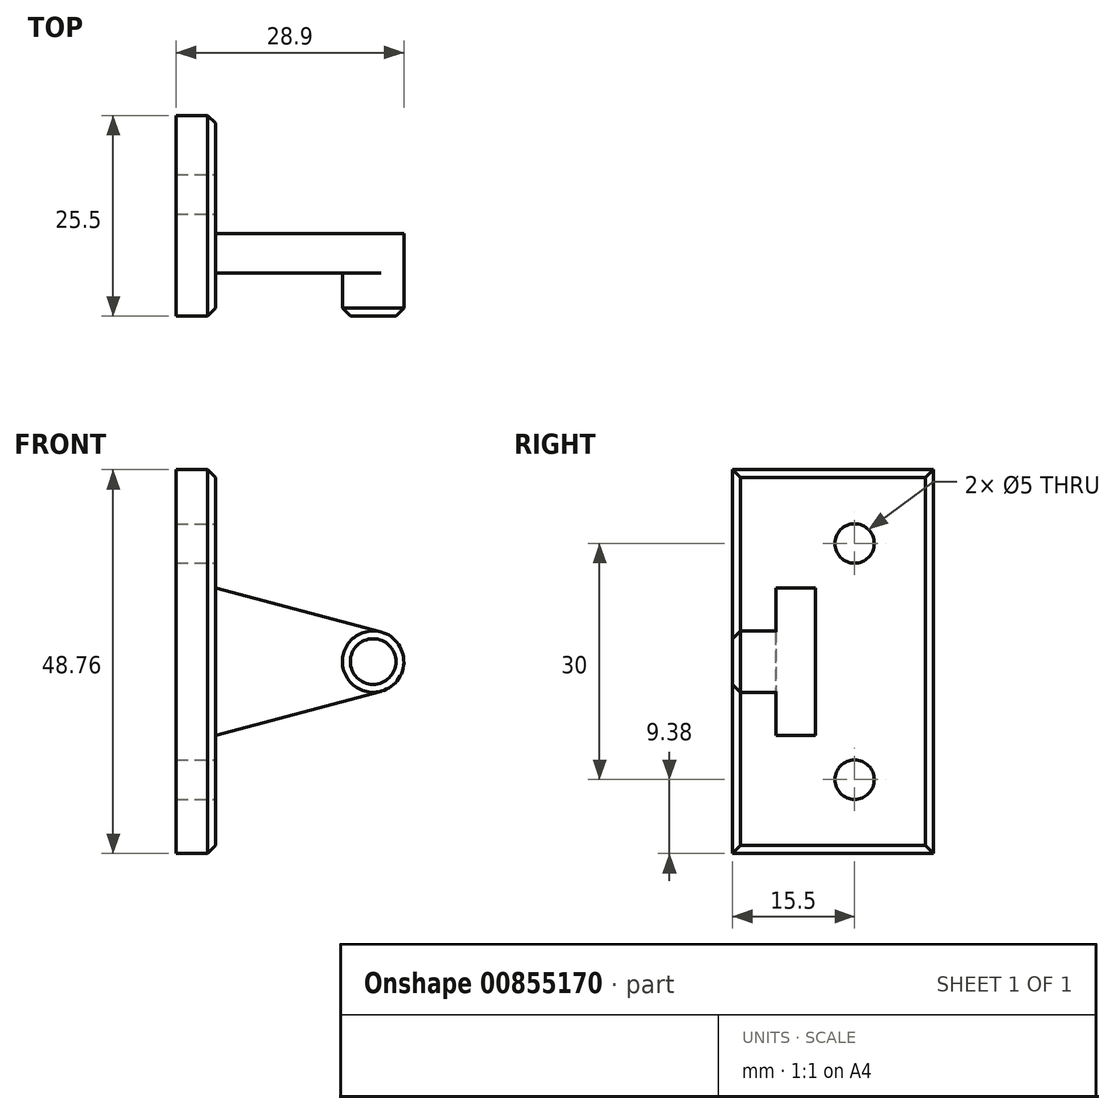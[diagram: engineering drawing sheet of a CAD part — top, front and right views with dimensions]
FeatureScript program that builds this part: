
annotation { "Feature Type Name" : "Feature", "Feature Type Description" : "" }
export const myFeature = defineFeature(function(context is Context, id is Id, definition is map)
    precondition{}
    {
        {
            var Q0;
            Q0=qCreatedBy(makeId("Front.planeOp"),FACE);
            var sketch = newSketch(context, id + "F0", { "sketchPlane" : qUnion([Q0])});
            skCircle(sketch, "E0", {"center": v(0, 0) * mm, "radius": 3.9 * mm});
            skLineSegment(sketch, "E1", {"start": v(-20, 0) * mm, "end": v(-20, 9.38) * mm});
            skLineSegment(sketch, "E2", {"start": v(-20, 0) * mm, "end": v(-20, -9.38) * mm});
            skLineSegment(sketch, "E3", {"start": v(-25, 0.78) * mm, "end": v(-25, -9.38) * mm});
            skLineSegment(sketch, "E4", {"start": v(-20, 9.38) * mm, "end": v(1, 3.77) * mm});
            skLineSegment(sketch, "E5", {"start": v(-20, -9.38) * mm, "end": v(1, -3.77) * mm});
            skLineSegment(sketch, "E6", {"start": v(-20, 9.38) * mm, "end": v(-20, 24.38) * mm});
            skLineSegment(sketch, "E7", {"start": v(-20, 24.38) * mm, "end": v(-25, 24.38) * mm});
            skLineSegment(sketch, "E8", {"start": v(-25, 24.38) * mm, "end": v(-25, 0.78) * mm});
            skLineSegment(sketch, "E9", {"start": v(-20, -9.38) * mm, "end": v(-20, -24.38) * mm});
            skLineSegment(sketch, "E10", {"start": v(-20, -24.38) * mm, "end": v(-25, -24.38) * mm});
            skLineSegment(sketch, "E11", {"start": v(-25, -24.38) * mm, "end": v(-25, -9.38) * mm});
            skSolve(sketch);
        }
        {
            var Q0;
            {var subQ0=sQuery(id+"F0.wireOp",EDGE,"E0");var subQ1=makeQuery(id+"F0.imprint","INTERSECT",VERTEX,{"derivedFrom":[subQ0,sQuery(id+"F0.wireOp",EDGE,"E4")]});Q0=makeQuery(id+"F0.imprint","IMPRINT",FACE,{"disambiguationData":[TD([[makeQuery(id+"F0.imprint","IMPRINT",EDGE,{"disambiguationData":[TD([[subQ1,-1.0]])],"derivedFrom":subQ0}),1.0]])]});}
            var Q1;
            Q1=makeQuery(id+"F0.imprint","IMPRINT",FACE,{"disambiguationData":[TD([[makeQuery(id+"F0.imprint","IMPRINT",EDGE,{"derivedFrom":sQuery(id+"F0.wireOp",EDGE,"E1")}),1.0]])]});
            extrude(context, id + "F1", {"entities" : qUnion([Q0, Q1]), "depth" : 5.5 * mm, "offsetDistance" : 25 * mm});
        }
        {
            var Q0;
            Q0=makeQuery(id+"F0.imprint","IMPRINT",FACE,{"disambiguationData":[TD([[makeQuery(id+"F0.imprint","IMPRINT",EDGE,{"derivedFrom":sQuery(id+"F0.wireOp",EDGE,"E1")}),-1.0]])]});
            var Q1;
            {var subQ0=sQuery(id+"F0.wireOp",EDGE,"E0");var subQ1=makeQuery(id+"F0.imprint","INTERSECT",VERTEX,{"derivedFrom":[subQ0,sQuery(id+"F0.wireOp",EDGE,"E4")]});Q1=makeQuery(id+"F0.imprint","IMPRINT",FACE,{"disambiguationData":[TD([[makeQuery(id+"F0.imprint","IMPRINT",EDGE,{"disambiguationData":[TD([[subQ1,-1.0]])],"derivedFrom":subQ0}),1.0]])]});}
            extrude(context, id + "F2", {"entities" : qUnion([Q0, Q1]), "operationType" : NewBodyOperationType.ADD, "oppositeDirection" : true, "depth" : 5 * mm, "offsetDistance" : 25 * mm});
        }
        {
            var Q0;
            Q0=makeQuery(id+"F0.imprint","IMPRINT",FACE,{"disambiguationData":[TD([[makeQuery(id+"F0.imprint","IMPRINT",EDGE,{"derivedFrom":sQuery(id+"F0.wireOp",EDGE,"E1")}),1.0]])]});
            extrude(context, id + "F3", {"entities" : qUnion([Q0]), "operationType" : NewBodyOperationType.ADD, "oppositeDirection" : true, "depth" : 20 * mm, "offsetDistance" : 25 * mm});
        }
        {
            var Q0;
            {var subQ0=sQuery(id+"F0.wireOp",EDGE,"E2");var subQ1=sQuery(id+"F0.wireOp",EDGE,"E1");Q0=makeQuery(id+"F3.boolean.opBoolean","MERGE",FACE,{"derivedFrom":[makeQuery(id+"F1.opExtrude","SWEPT_FACE",FACE,{"disambiguationData":[OSD([subQ1,subQ0])]}),makeQuery(id+"F3.opExtrude","SWEPT_FACE",FACE,{"disambiguationData":[OSD([subQ1,subQ0])]})]});}
            var sketch = newSketch(context, id + "F4", { "sketchPlane" : qUnion([Q0])});
            skPoint(sketch, "E12", {"position": v(10, 0) * mm});
            skPoint(sketch, "E13", {"position": v(10, 15) * mm});
            skPoint(sketch, "E14", {"position": v(10, -15) * mm});
            skCircle(sketch, "E15", {"center": v(10, 15) * mm, "radius": 2.5 * mm});
            skCircle(sketch, "E16", {"center": v(10, -15) * mm, "radius": 2.5 * mm});
            skSolve(sketch);
        }
        {
            var Q0;
            Q0=makeQuery(id+"F4.imprint","IMPRINT",FACE,{"disambiguationData":[TD([[makeQuery(id+"F4.imprint","IMPRINT",EDGE,{"derivedFrom":sQuery(id+"F4.wireOp",EDGE,"E15")}),1.0]])]});
            var Q1;
            Q1=makeQuery(id+"F4.imprint","IMPRINT",FACE,{"disambiguationData":[TD([[makeQuery(id+"F4.imprint","IMPRINT",EDGE,{"derivedFrom":sQuery(id+"F4.wireOp",EDGE,"E16")}),1.0]])]});
            extrude(context, id + "F5", {"entities" : qUnion([Q0, Q1]), "operationType" : NewBodyOperationType.REMOVE, "oppositeDirection" : true, "depth" : 10 * mm, "offsetDistance" : 25 * mm});
        }
        {
            var Q0;
            Q0=makeQuery(id+"F5.boolean.opBoolean","COPY",EDGE,{"derivedFrom":makeQuery(id+"F5.opExtrude","CAP_EDGE",EDGE,{"disambiguationData":[OSD([sQuery(id+"F4.wireOp",EDGE,"E15")])],"isStart":true})});
            var Q1;
            Q1=makeQuery(id+"F5.boolean.opBoolean","COPY",EDGE,{"derivedFrom":makeQuery(id+"F5.opExtrude","CAP_EDGE",EDGE,{"disambiguationData":[OSD([sQuery(id+"F4.wireOp",EDGE,"E16")])],"isStart":true})});
            var Q2;
            Q2=makeQuery(id+"F1.opExtrude","CAP_FACE",FACE,{"disambiguationData":[OSD([sQuery(id+"F0.wireOp",EDGE,"E0")])],"isStart":false});
            var Q3;
            Q3=makeQuery(id+"F3.opExtrude","CAP_EDGE",EDGE,{"disambiguationData":[OSD([sQuery(id+"F0.wireOp",EDGE,"E1"),sQuery(id+"F0.wireOp",EDGE,"E2"),sQuery(id+"F0.wireOp",EDGE,"E6"),sQuery(id+"F0.wireOp",EDGE,"E9")])],"isStart":false});
            var Q4;
            {var subQ0=sQuery(id+"F0.wireOp",EDGE,"E7");var subQ1=sQuery(id+"F0.wireOp",EDGE,"E6");Q4=makeQuery(id+"F3.boolean.opBoolean","MERGE",EDGE,{"derivedFrom":[makeQuery(id+"F1.opExtrude","SWEPT_EDGE",EDGE,{"disambiguationData":[OSD([subQ1,subQ0])]}),makeQuery(id+"F3.opExtrude","SWEPT_EDGE",EDGE,{"disambiguationData":[OSD([subQ1,subQ0])]})]});}
            var Q5;
            Q5=makeQuery(id+"F1.opExtrude","CAP_EDGE",EDGE,{"disambiguationData":[OSD([sQuery(id+"F0.wireOp",EDGE,"E1"),sQuery(id+"F0.wireOp",EDGE,"E2"),sQuery(id+"F0.wireOp",EDGE,"E6"),sQuery(id+"F0.wireOp",EDGE,"E9")])],"isStart":false});
            var Q6;
            {var subQ0=sQuery(id+"F0.wireOp",EDGE,"E10");var subQ1=sQuery(id+"F0.wireOp",EDGE,"E9");Q6=makeQuery(id+"F3.boolean.opBoolean","MERGE",EDGE,{"derivedFrom":[makeQuery(id+"F1.opExtrude","SWEPT_EDGE",EDGE,{"disambiguationData":[OSD([subQ1,subQ0])]}),makeQuery(id+"F3.opExtrude","SWEPT_EDGE",EDGE,{"disambiguationData":[OSD([subQ1,subQ0])]})]});}
            chamfer(context, id + "F6", {"entities" : qUnion([Q0, Q1, Q2, Q3, Q4, Q5, Q6]), "width" : 1 * mm, "tangentPropagation" : true});
        }
    });
